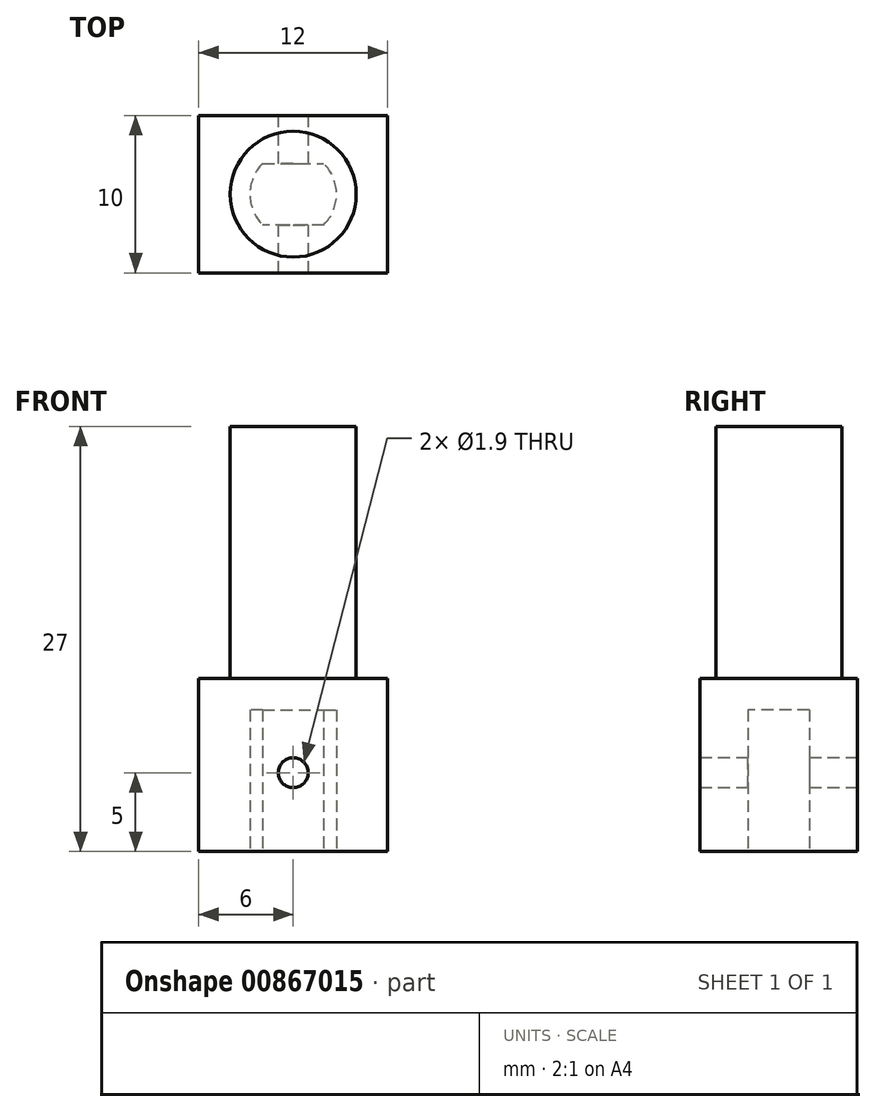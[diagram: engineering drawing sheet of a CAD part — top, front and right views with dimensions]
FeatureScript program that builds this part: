
annotation { "Feature Type Name" : "Feature", "Feature Type Description" : "" }
export const myFeature = defineFeature(function(context is Context, id is Id, definition is map)
    precondition{}
    {
        {
            var Q0;
            Q0=qCreatedBy(makeId("Top.planeOp"),FACE);
            var sketch = newSketch(context, id + "F0", { "sketchPlane" : qUnion([Q0])});
            skArc(sketch, "E0", {"start": v(-1.94, 1.95) * mm, "mid": v(-2.75, 0) * mm, "end": v(-1.94, -1.95) * mm});
            skLineSegment(sketch, "E1", {"start": v(-1.94, 1.95) * mm, "end": v(1.94, 1.95) * mm});
            skLineSegment(sketch, "E2", {"start": v(1.94, -1.95) * mm, "end": v(-1.94, -1.95) * mm});
            skLineSegment(sketch, "E3", {"start": v(-2.75, 0) * mm, "end": v(2.75, 0) * mm, "construction": true});
            skArc(sketch, "E4.trimOffspring", {"start": v(1.94, -1.95) * mm, "mid": v(2.75, 0) * mm, "end": v(1.94, 1.95) * mm});
            skLineSegment(sketch, "E5.bottom", {"start": v(6, 5) * mm, "end": v(-6, 5) * mm});
            skLineSegment(sketch, "E5.top", {"start": v(6, -5) * mm, "end": v(-6, -5) * mm});
            skLineSegment(sketch, "E5.left", {"start": v(6, 5) * mm, "end": v(6, -5) * mm});
            skLineSegment(sketch, "E5.right", {"start": v(-6, 5) * mm, "end": v(-6, -5) * mm});
            skSolve(sketch);
        }
        {
            var Q0;
            Q0 = qSketchRegion(id + "F0", true);
            extrude(context, id + "F1", {"entities" : qUnion([Q0]), "depth" : 9 * mm, "offsetDistance" : 25 * mm});
        }
        {
            var Q0;
            Q0=makeQuery(id+"F1.opExtrude","SWEPT_FACE",FACE,{"disambiguationData":[OSD([sQuery(id+"F0.wireOp",EDGE,"E5.top")])]});
            var sketch = newSketch(context, id + "F2", { "sketchPlane" : qUnion([Q0])});
            skCircle(sketch, "E6", {"center": v(0, 5) * mm, "radius": 0.95 * mm});
            skSolve(sketch);
        }
        {
            var Q0;
            Q0 = qSketchRegion(id + "F2", true);
            var Q1;
            Q1=makeQuery(id+"F1.opExtrude","SWEPT_FACE",FACE,{"disambiguationData":[OSD([sQuery(id+"F0.wireOp",EDGE,"E5.bottom")])]});
            extrude(context, id + "F3", {"entities" : qUnion([Q0]), "operationType" : NewBodyOperationType.REMOVE, "endBound" : BoundingType.UP_TO_SURFACE, "oppositeDirection" : true, "depth" : 25 * mm, "endBoundEntityFace" : qUnion([Q1]), "offsetDistance" : 25 * mm});
        }
        {
            var Q0;
            Q0=makeQuery(id+"F1.opExtrude","CAP_FACE",FACE,{"disambiguationData":[OSD([sQuery(id+"F0.wireOp",EDGE,"E0"),sQuery(id+"F0.wireOp",EDGE,"E1"),sQuery(id+"F0.wireOp",EDGE,"E2"),sQuery(id+"F0.wireOp",EDGE,"E4.trimOffspring"),sQuery(id+"F0.wireOp",EDGE,"E5.bottom"),sQuery(id+"F0.wireOp",EDGE,"E5.top"),sQuery(id+"F0.wireOp",EDGE,"E5.left"),sQuery(id+"F0.wireOp",EDGE,"E5.right")])],"isStart":false});
            var sketch = newSketch(context, id + "F4", { "sketchPlane" : qUnion([Q0])});
            skLineSegment(sketch, "E7.bottom", {"start": v(-6, -5) * mm, "end": v(6, -5) * mm});
            skLineSegment(sketch, "E7.top", {"start": v(-6, 5) * mm, "end": v(6, 5) * mm});
            skLineSegment(sketch, "E7.left", {"start": v(-6, -5) * mm, "end": v(-6, 5) * mm});
            skLineSegment(sketch, "E7.right", {"start": v(6, -5) * mm, "end": v(6, 5) * mm});
            skSolve(sketch);
        }
        {
            var Q0;
            Q0 = qSketchRegion(id + "F4", true);
            extrude(context, id + "F5", {"entities" : qUnion([Q0]), "operationType" : NewBodyOperationType.ADD, "depth" : 2 * mm, "offsetDistance" : 25 * mm});
        }
        {
            var Q0;
            Q0=makeQuery(id+"F5.opExtrude","CAP_FACE",FACE,{"disambiguationData":[OSD([sQuery(id+"F4.wireOp",EDGE,"E7.bottom"),sQuery(id+"F4.wireOp",EDGE,"E7.top"),sQuery(id+"F4.wireOp",EDGE,"E7.left"),sQuery(id+"F4.wireOp",EDGE,"E7.right")])],"isStart":false});
            var sketch = newSketch(context, id + "F6", { "sketchPlane" : qUnion([Q0])});
            skCircle(sketch, "E8", {"center": v(0, 0) * mm, "radius": 4 * mm});
            skSolve(sketch);
        }
        {
            var Q0;
            Q0 = qSketchRegion(id + "F6", true);
            extrude(context, id + "F7", {"entities" : qUnion([Q0]), "operationType" : NewBodyOperationType.ADD, "depth" : 16 * mm, "offsetDistance" : 25 * mm});
        }
    });
